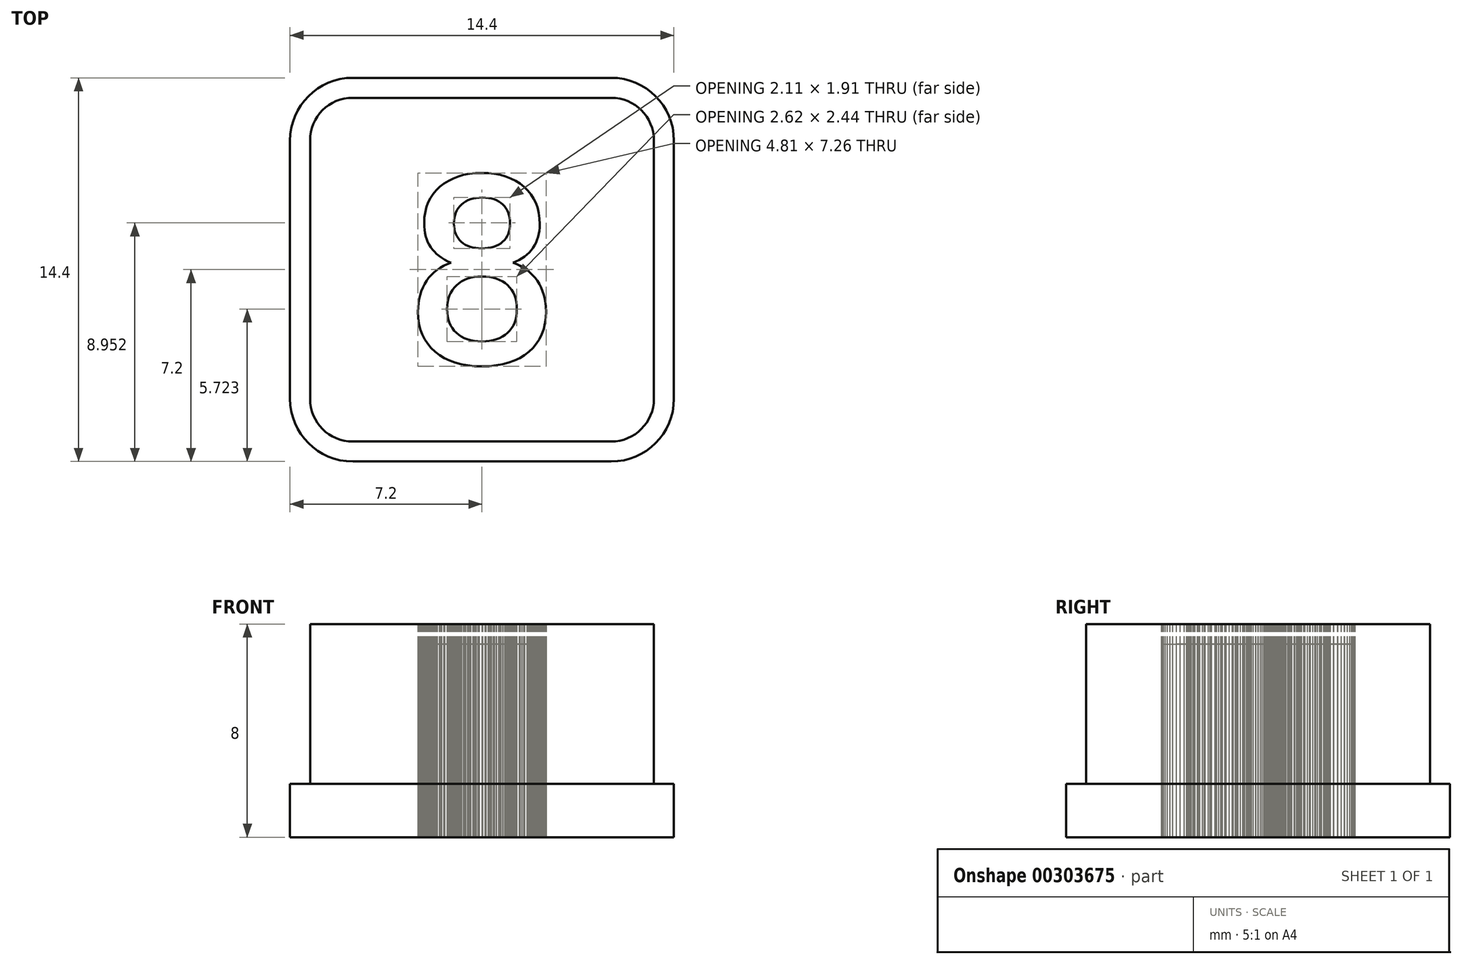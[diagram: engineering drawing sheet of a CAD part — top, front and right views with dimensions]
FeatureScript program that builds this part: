
annotation { "Feature Type Name" : "Feature", "Feature Type Description" : "" }
export const myFeature = defineFeature(function(context is Context, id is Id, definition is map)
    precondition{}
    {
        {
            var Q0;
            Q0=qCreatedBy(makeId("Top.planeOp"),FACE);
            var sketch = newSketch(context, id + "F0", { "sketchPlane" : qUnion([Q0])});
            skArc(sketch, "E0", {"start": v(4.85, -6.45) * mm, "mid": v(5.98, -5.98) * mm, "end": v(6.45, -4.85) * mm});
            skLineSegment(sketch, "E1", {"start": v(6.45, -4.85) * mm, "end": v(6.45, 4.85) * mm});
            skArc(sketch, "E2", {"start": v(6.45, 4.85) * mm, "mid": v(5.98, 5.98) * mm, "end": v(4.85, 6.45) * mm});
            skLineSegment(sketch, "E3", {"start": v(4.85, 6.45) * mm, "end": v(-4.85, 6.45) * mm});
            skArc(sketch, "E4", {"start": v(-4.85, 6.45) * mm, "mid": v(-5.98, 5.98) * mm, "end": v(-6.45, 4.85) * mm});
            skLineSegment(sketch, "E5", {"start": v(-6.45, 4.85) * mm, "end": v(-6.45, -4.85) * mm});
            skArc(sketch, "E6", {"start": v(-6.45, -4.85) * mm, "mid": v(-5.98, -5.98) * mm, "end": v(-4.85, -6.45) * mm});
            skLineSegment(sketch, "E7", {"start": v(-4.85, -6.45) * mm, "end": v(4.85, -6.45) * mm});
            skArc(sketch, "E8", {"start": v(-4.85, 7.2) * mm, "mid": v(-6.51, 6.51) * mm, "end": v(-7.2, 4.85) * mm});
            skLineSegment(sketch, "E9", {"start": v(-7.2, 4.85) * mm, "end": v(-7.2, -4.85) * mm});
            skArc(sketch, "E10", {"start": v(-7.2, -4.85) * mm, "mid": v(-6.51, -6.51) * mm, "end": v(-4.85, -7.2) * mm});
            skLineSegment(sketch, "E11", {"start": v(-4.85, -7.2) * mm, "end": v(4.85, -7.2) * mm});
            skArc(sketch, "E12", {"start": v(4.85, -7.2) * mm, "mid": v(6.51, -6.51) * mm, "end": v(7.2, -4.85) * mm});
            skLineSegment(sketch, "E13", {"start": v(7.2, -4.85) * mm, "end": v(7.2, 4.85) * mm});
            skArc(sketch, "E14", {"start": v(7.2, 4.85) * mm, "mid": v(6.51, 6.51) * mm, "end": v(4.85, 7.2) * mm});
            skLineSegment(sketch, "E15", {"start": v(4.85, 7.2) * mm, "end": v(-4.85, 7.2) * mm});
            skLineSegment(sketch, "E16", {"start": v(-1.16, 0.26) * mm, "end": v(-1.29, 0.32) * mm});
            skLineSegment(sketch, "E17", {"start": v(-1.29, 0.32) * mm, "end": v(-1.4, 0.38) * mm});
            skLineSegment(sketch, "E18", {"start": v(-1.4, 0.38) * mm, "end": v(-1.51, 0.45) * mm});
            skLineSegment(sketch, "E19", {"start": v(-1.51, 0.45) * mm, "end": v(-1.61, 0.52) * mm});
            skLineSegment(sketch, "E20", {"start": v(-1.61, 0.52) * mm, "end": v(-1.7, 0.6) * mm});
            skLineSegment(sketch, "E21", {"start": v(-1.7, 0.6) * mm, "end": v(-1.79, 0.67) * mm});
            skLineSegment(sketch, "E22", {"start": v(-1.79, 0.67) * mm, "end": v(-1.86, 0.76) * mm});
            skLineSegment(sketch, "E23", {"start": v(-1.86, 0.76) * mm, "end": v(-1.92, 0.85) * mm});
            skLineSegment(sketch, "E24", {"start": v(-1.92, 0.85) * mm, "end": v(-1.98, 0.94) * mm});
            skLineSegment(sketch, "E25", {"start": v(-1.98, 0.94) * mm, "end": v(-2.03, 1.04) * mm});
            skLineSegment(sketch, "E26", {"start": v(-2.03, 1.04) * mm, "end": v(-2.07, 1.14) * mm});
            skLineSegment(sketch, "E27", {"start": v(-2.07, 1.14) * mm, "end": v(-2.1, 1.26) * mm});
            skLineSegment(sketch, "E28", {"start": v(-2.1, 1.26) * mm, "end": v(-2.13, 1.37) * mm});
            skLineSegment(sketch, "E29", {"start": v(-2.13, 1.37) * mm, "end": v(-2.15, 1.5) * mm});
            skLineSegment(sketch, "E30", {"start": v(-2.15, 1.5) * mm, "end": v(-2.16, 1.62) * mm});
            skLineSegment(sketch, "E31", {"start": v(-2.16, 1.62) * mm, "end": v(-2.17, 1.75) * mm});
            skLineSegment(sketch, "E32", {"start": v(-2.17, 1.75) * mm, "end": v(-2.16, 1.96) * mm});
            skLineSegment(sketch, "E33", {"start": v(-2.16, 1.96) * mm, "end": v(-2.13, 2.16) * mm});
            skLineSegment(sketch, "E34", {"start": v(-2.13, 2.16) * mm, "end": v(-2.08, 2.34) * mm});
            skLineSegment(sketch, "E35", {"start": v(-2.08, 2.34) * mm, "end": v(-2.02, 2.52) * mm});
            skLineSegment(sketch, "E36", {"start": v(-2.02, 2.52) * mm, "end": v(-1.94, 2.68) * mm});
            skLineSegment(sketch, "E37", {"start": v(-1.94, 2.68) * mm, "end": v(-1.83, 2.83) * mm});
            skLineSegment(sketch, "E38", {"start": v(-1.83, 2.83) * mm, "end": v(-1.71, 2.98) * mm});
            skLineSegment(sketch, "E39", {"start": v(-1.71, 2.98) * mm, "end": v(-1.58, 3.11) * mm});
            skLineSegment(sketch, "E40", {"start": v(-1.58, 3.11) * mm, "end": v(-1.42, 3.23) * mm});
            skLineSegment(sketch, "E41", {"start": v(-1.42, 3.23) * mm, "end": v(-1.26, 3.34) * mm});
            skLineSegment(sketch, "E42", {"start": v(-1.26, 3.34) * mm, "end": v(-1.08, 3.43) * mm});
            skLineSegment(sketch, "E43", {"start": v(-1.08, 3.43) * mm, "end": v(-0.89, 3.5) * mm});
            skLineSegment(sketch, "E44", {"start": v(-0.89, 3.5) * mm, "end": v(-0.68, 3.56) * mm});
            skLineSegment(sketch, "E45", {"start": v(-0.68, 3.56) * mm, "end": v(-0.47, 3.6) * mm});
            skLineSegment(sketch, "E46", {"start": v(-0.47, 3.6) * mm, "end": v(-0.25, 3.62) * mm});
            skLineSegment(sketch, "E47", {"start": v(-0.25, 3.62) * mm, "end": v(0, 3.63) * mm});
            skLineSegment(sketch, "E48", {"start": v(0, 3.63) * mm, "end": v(0.24, 3.62) * mm});
            skLineSegment(sketch, "E49", {"start": v(0.24, 3.62) * mm, "end": v(0.47, 3.6) * mm});
            skLineSegment(sketch, "E50", {"start": v(0.47, 3.6) * mm, "end": v(0.68, 3.56) * mm});
            skLineSegment(sketch, "E51", {"start": v(0.68, 3.56) * mm, "end": v(0.89, 3.5) * mm});
            skLineSegment(sketch, "E52", {"start": v(0.89, 3.5) * mm, "end": v(1.08, 3.42) * mm});
            skLineSegment(sketch, "E53", {"start": v(1.08, 3.42) * mm, "end": v(1.26, 3.33) * mm});
            skLineSegment(sketch, "E54", {"start": v(1.26, 3.33) * mm, "end": v(1.43, 3.23) * mm});
            skLineSegment(sketch, "E55", {"start": v(1.43, 3.23) * mm, "end": v(1.58, 3.1) * mm});
            skLineSegment(sketch, "E56", {"start": v(1.58, 3.1) * mm, "end": v(1.72, 2.97) * mm});
            skLineSegment(sketch, "E57", {"start": v(1.72, 2.97) * mm, "end": v(1.84, 2.82) * mm});
            skLineSegment(sketch, "E58", {"start": v(1.84, 2.82) * mm, "end": v(1.94, 2.66) * mm});
            skLineSegment(sketch, "E59", {"start": v(1.94, 2.66) * mm, "end": v(2.02, 2.5) * mm});
            skLineSegment(sketch, "E60", {"start": v(2.02, 2.5) * mm, "end": v(2.09, 2.31) * mm});
            skLineSegment(sketch, "E61", {"start": v(2.09, 2.31) * mm, "end": v(2.13, 2.12) * mm});
            skLineSegment(sketch, "E62", {"start": v(2.13, 2.12) * mm, "end": v(2.16, 1.92) * mm});
            skLineSegment(sketch, "E63", {"start": v(2.16, 1.92) * mm, "end": v(2.17, 1.7) * mm});
            skLineSegment(sketch, "E64", {"start": v(2.17, 1.7) * mm, "end": v(2.16, 1.58) * mm});
            skLineSegment(sketch, "E65", {"start": v(2.16, 1.58) * mm, "end": v(2.15, 1.46) * mm});
            skLineSegment(sketch, "E66", {"start": v(2.15, 1.46) * mm, "end": v(2.13, 1.34) * mm});
            skLineSegment(sketch, "E67", {"start": v(2.13, 1.34) * mm, "end": v(2.1, 1.23) * mm});
            skLineSegment(sketch, "E68", {"start": v(2.1, 1.23) * mm, "end": v(2.07, 1.12) * mm});
            skLineSegment(sketch, "E69", {"start": v(2.07, 1.12) * mm, "end": v(2.02, 1.01) * mm});
            skLineSegment(sketch, "E70", {"start": v(2.02, 1.01) * mm, "end": v(1.97, 0.91) * mm});
            skLineSegment(sketch, "E71", {"start": v(1.97, 0.91) * mm, "end": v(1.91, 0.82) * mm});
            skLineSegment(sketch, "E72", {"start": v(1.91, 0.82) * mm, "end": v(1.84, 0.73) * mm});
            skLineSegment(sketch, "E73", {"start": v(1.84, 0.73) * mm, "end": v(1.77, 0.65) * mm});
            skLineSegment(sketch, "E74", {"start": v(1.77, 0.65) * mm, "end": v(1.69, 0.57) * mm});
            skLineSegment(sketch, "E75", {"start": v(1.69, 0.57) * mm, "end": v(1.6, 0.5) * mm});
            skLineSegment(sketch, "E76", {"start": v(1.6, 0.5) * mm, "end": v(1.5, 0.43) * mm});
            skLineSegment(sketch, "E77", {"start": v(1.5, 0.43) * mm, "end": v(1.4, 0.37) * mm});
            skLineSegment(sketch, "E78", {"start": v(1.4, 0.37) * mm, "end": v(1.28, 0.3) * mm});
            skLineSegment(sketch, "E79", {"start": v(1.28, 0.3) * mm, "end": v(1.16, 0.26) * mm});
            skLineSegment(sketch, "E80", {"start": v(1.16, 0.26) * mm, "end": v(1.3, 0.2) * mm});
            skLineSegment(sketch, "E81", {"start": v(1.3, 0.2) * mm, "end": v(1.44, 0.14) * mm});
            skLineSegment(sketch, "E82", {"start": v(1.44, 0.14) * mm, "end": v(1.56, 0.07) * mm});
            skLineSegment(sketch, "E83", {"start": v(1.56, 0.07) * mm, "end": v(1.68, 0) * mm});
            skLineSegment(sketch, "E84", {"start": v(1.68, 0) * mm, "end": v(1.79, -0.1) * mm});
            skLineSegment(sketch, "E85", {"start": v(1.79, -0.1) * mm, "end": v(1.9, -0.2) * mm});
            skLineSegment(sketch, "E86", {"start": v(1.9, -0.2) * mm, "end": v(1.99, -0.3) * mm});
            skLineSegment(sketch, "E87", {"start": v(1.99, -0.3) * mm, "end": v(2.07, -0.42) * mm});
            skLineSegment(sketch, "E88", {"start": v(2.07, -0.42) * mm, "end": v(2.15, -0.54) * mm});
            skLineSegment(sketch, "E89", {"start": v(2.15, -0.54) * mm, "end": v(2.22, -0.67) * mm});
            skLineSegment(sketch, "E90", {"start": v(2.22, -0.67) * mm, "end": v(2.27, -0.8) * mm});
            skLineSegment(sketch, "E91", {"start": v(2.27, -0.8) * mm, "end": v(2.32, -0.95) * mm});
            skLineSegment(sketch, "E92", {"start": v(2.32, -0.95) * mm, "end": v(2.36, -1.1) * mm});
            skLineSegment(sketch, "E93", {"start": v(2.36, -1.1) * mm, "end": v(2.38, -1.24) * mm});
            skLineSegment(sketch, "E94", {"start": v(2.38, -1.24) * mm, "end": v(2.4, -1.4) * mm});
            skLineSegment(sketch, "E95", {"start": v(2.4, -1.4) * mm, "end": v(2.4, -1.56) * mm});
            skLineSegment(sketch, "E96", {"start": v(2.4, -1.56) * mm, "end": v(2.4, -1.8) * mm});
            skLineSegment(sketch, "E97", {"start": v(2.4, -1.8) * mm, "end": v(2.36, -2.02) * mm});
            skLineSegment(sketch, "E98", {"start": v(2.36, -2.02) * mm, "end": v(2.31, -2.23) * mm});
            skLineSegment(sketch, "E99", {"start": v(2.31, -2.23) * mm, "end": v(2.24, -2.43) * mm});
            skLineSegment(sketch, "E100", {"start": v(2.24, -2.43) * mm, "end": v(2.15, -2.6) * mm});
            skLineSegment(sketch, "E101", {"start": v(2.15, -2.6) * mm, "end": v(2.04, -2.78) * mm});
            skLineSegment(sketch, "E102", {"start": v(2.04, -2.78) * mm, "end": v(1.91, -2.94) * mm});
            skLineSegment(sketch, "E103", {"start": v(1.91, -2.94) * mm, "end": v(1.76, -3.08) * mm});
            skLineSegment(sketch, "E104", {"start": v(1.76, -3.08) * mm, "end": v(1.6, -3.2) * mm});
            skLineSegment(sketch, "E105", {"start": v(1.6, -3.2) * mm, "end": v(1.41, -3.32) * mm});
            skLineSegment(sketch, "E106", {"start": v(1.41, -3.32) * mm, "end": v(1.22, -3.41) * mm});
            skLineSegment(sketch, "E107", {"start": v(1.22, -3.41) * mm, "end": v(1, -3.5) * mm});
            skLineSegment(sketch, "E108", {"start": v(1, -3.5) * mm, "end": v(0.77, -3.55) * mm});
            skLineSegment(sketch, "E109", {"start": v(0.77, -3.55) * mm, "end": v(0.53, -3.6) * mm});
            skLineSegment(sketch, "E110", {"start": v(0.53, -3.6) * mm, "end": v(0.27, -3.62) * mm});
            skLineSegment(sketch, "E111", {"start": v(0.27, -3.62) * mm, "end": v(0, -3.63) * mm});
            skLineSegment(sketch, "E112", {"start": v(0, -3.63) * mm, "end": v(-0.28, -3.62) * mm});
            skLineSegment(sketch, "E113", {"start": v(-0.28, -3.62) * mm, "end": v(-0.53, -3.6) * mm});
            skLineSegment(sketch, "E114", {"start": v(-0.53, -3.6) * mm, "end": v(-0.78, -3.55) * mm});
            skLineSegment(sketch, "E115", {"start": v(-0.78, -3.55) * mm, "end": v(-1, -3.5) * mm});
            skLineSegment(sketch, "E116", {"start": v(-1, -3.5) * mm, "end": v(-1.21, -3.41) * mm});
            skLineSegment(sketch, "E117", {"start": v(-1.21, -3.41) * mm, "end": v(-1.41, -3.32) * mm});
            skLineSegment(sketch, "E118", {"start": v(-1.41, -3.32) * mm, "end": v(-1.6, -3.2) * mm});
            skLineSegment(sketch, "E119", {"start": v(-1.6, -3.2) * mm, "end": v(-1.76, -3.08) * mm});
            skLineSegment(sketch, "E120", {"start": v(-1.76, -3.08) * mm, "end": v(-1.91, -2.94) * mm});
            skLineSegment(sketch, "E121", {"start": v(-1.91, -2.94) * mm, "end": v(-2.04, -2.78) * mm});
            skLineSegment(sketch, "E122", {"start": v(-2.04, -2.78) * mm, "end": v(-2.15, -2.61) * mm});
            skLineSegment(sketch, "E123", {"start": v(-2.15, -2.61) * mm, "end": v(-2.24, -2.43) * mm});
            skLineSegment(sketch, "E124", {"start": v(-2.24, -2.43) * mm, "end": v(-2.31, -2.24) * mm});
            skLineSegment(sketch, "E125", {"start": v(-2.31, -2.24) * mm, "end": v(-2.36, -2.03) * mm});
            skLineSegment(sketch, "E126", {"start": v(-2.36, -2.03) * mm, "end": v(-2.4, -1.81) * mm});
            skLineSegment(sketch, "E127", {"start": v(-2.4, -1.81) * mm, "end": v(-2.4, -1.58) * mm});
            skLineSegment(sketch, "E128", {"start": v(-2.4, -1.58) * mm, "end": v(-2.4, -1.41) * mm});
            skLineSegment(sketch, "E129", {"start": v(-2.4, -1.41) * mm, "end": v(-2.38, -1.25) * mm});
            skLineSegment(sketch, "E130", {"start": v(-2.38, -1.25) * mm, "end": v(-2.36, -1.1) * mm});
            skLineSegment(sketch, "E131", {"start": v(-2.36, -1.1) * mm, "end": v(-2.32, -0.95) * mm});
            skLineSegment(sketch, "E132", {"start": v(-2.32, -0.95) * mm, "end": v(-2.28, -0.8) * mm});
            skLineSegment(sketch, "E133", {"start": v(-2.28, -0.8) * mm, "end": v(-2.22, -0.67) * mm});
            skLineSegment(sketch, "E134", {"start": v(-2.22, -0.67) * mm, "end": v(-2.15, -0.54) * mm});
            skLineSegment(sketch, "E135", {"start": v(-2.15, -0.54) * mm, "end": v(-2.08, -0.41) * mm});
            skLineSegment(sketch, "E136", {"start": v(-2.08, -0.41) * mm, "end": v(-2, -0.3) * mm});
            skLineSegment(sketch, "E137", {"start": v(-2, -0.3) * mm, "end": v(-1.9, -0.2) * mm});
            skLineSegment(sketch, "E138", {"start": v(-1.9, -0.2) * mm, "end": v(-1.8, -0.1) * mm});
            skLineSegment(sketch, "E139", {"start": v(-1.8, -0.1) * mm, "end": v(-1.69, 0) * mm});
            skLineSegment(sketch, "E140", {"start": v(-1.69, 0) * mm, "end": v(-1.57, 0.07) * mm});
            skLineSegment(sketch, "E141", {"start": v(-1.57, 0.07) * mm, "end": v(-1.44, 0.14) * mm});
            skLineSegment(sketch, "E142", {"start": v(-1.44, 0.14) * mm, "end": v(-1.3, 0.2) * mm});
            skLineSegment(sketch, "E143", {"start": v(-1.3, 0.2) * mm, "end": v(-1.16, 0.26) * mm});
            skLineSegment(sketch, "E144", {"start": v(0.02, 2.7) * mm, "end": v(-0.1, 2.7) * mm});
            skLineSegment(sketch, "E145", {"start": v(-0.1, 2.7) * mm, "end": v(-0.22, 2.69) * mm});
            skLineSegment(sketch, "E146", {"start": v(-0.22, 2.69) * mm, "end": v(-0.33, 2.67) * mm});
            skLineSegment(sketch, "E147", {"start": v(-0.33, 2.67) * mm, "end": v(-0.43, 2.64) * mm});
            skLineSegment(sketch, "E148", {"start": v(-0.43, 2.64) * mm, "end": v(-0.52, 2.6) * mm});
            skLineSegment(sketch, "E149", {"start": v(-0.52, 2.6) * mm, "end": v(-0.61, 2.56) * mm});
            skLineSegment(sketch, "E150", {"start": v(-0.61, 2.56) * mm, "end": v(-0.7, 2.5) * mm});
            skLineSegment(sketch, "E151", {"start": v(-0.7, 2.5) * mm, "end": v(-0.77, 2.45) * mm});
            skLineSegment(sketch, "E152", {"start": v(-0.77, 2.45) * mm, "end": v(-0.83, 2.38) * mm});
            skLineSegment(sketch, "E153", {"start": v(-0.83, 2.38) * mm, "end": v(-0.9, 2.3) * mm});
            skLineSegment(sketch, "E154", {"start": v(-0.9, 2.3) * mm, "end": v(-0.94, 2.22) * mm});
            skLineSegment(sketch, "E155", {"start": v(-0.94, 2.22) * mm, "end": v(-0.98, 2.14) * mm});
            skLineSegment(sketch, "E156", {"start": v(-0.98, 2.14) * mm, "end": v(-1.01, 2.05) * mm});
            skLineSegment(sketch, "E157", {"start": v(-1.01, 2.05) * mm, "end": v(-1.04, 1.95) * mm});
            skLineSegment(sketch, "E158", {"start": v(-1.04, 1.95) * mm, "end": v(-1.05, 1.85) * mm});
            skLineSegment(sketch, "E159", {"start": v(-1.05, 1.85) * mm, "end": v(-1.05, 1.74) * mm});
            skLineSegment(sketch, "E160", {"start": v(-1.05, 1.74) * mm, "end": v(-1.05, 1.63) * mm});
            skLineSegment(sketch, "E161", {"start": v(-1.05, 1.63) * mm, "end": v(-1.04, 1.53) * mm});
            skLineSegment(sketch, "E162", {"start": v(-1.04, 1.53) * mm, "end": v(-1.01, 1.43) * mm});
            skLineSegment(sketch, "E163", {"start": v(-1.01, 1.43) * mm, "end": v(-0.98, 1.34) * mm});
            skLineSegment(sketch, "E164", {"start": v(-0.98, 1.34) * mm, "end": v(-0.95, 1.26) * mm});
            skLineSegment(sketch, "E165", {"start": v(-0.95, 1.26) * mm, "end": v(-0.9, 1.18) * mm});
            skLineSegment(sketch, "E166", {"start": v(-0.9, 1.18) * mm, "end": v(-0.84, 1.11) * mm});
            skLineSegment(sketch, "E167", {"start": v(-0.84, 1.11) * mm, "end": v(-0.77, 1.05) * mm});
            skLineSegment(sketch, "E168", {"start": v(-0.77, 1.05) * mm, "end": v(-0.7, 0.99) * mm});
            skLineSegment(sketch, "E169", {"start": v(-0.7, 0.99) * mm, "end": v(-0.62, 0.94) * mm});
            skLineSegment(sketch, "E170", {"start": v(-0.62, 0.94) * mm, "end": v(-0.54, 0.9) * mm});
            skLineSegment(sketch, "E171", {"start": v(-0.54, 0.9) * mm, "end": v(-0.44, 0.86) * mm});
            skLineSegment(sketch, "E172", {"start": v(-0.44, 0.86) * mm, "end": v(-0.34, 0.83) * mm});
            skLineSegment(sketch, "E173", {"start": v(-0.34, 0.83) * mm, "end": v(-0.24, 0.81) * mm});
            skLineSegment(sketch, "E174", {"start": v(-0.24, 0.81) * mm, "end": v(-0.13, 0.8) * mm});
            skLineSegment(sketch, "E175", {"start": v(-0.13, 0.8) * mm, "end": v(0, 0.8) * mm});
            skLineSegment(sketch, "E176", {"start": v(0, 0.8) * mm, "end": v(0.11, 0.8) * mm});
            skLineSegment(sketch, "E177", {"start": v(0.11, 0.8) * mm, "end": v(0.23, 0.81) * mm});
            skLineSegment(sketch, "E178", {"start": v(0.23, 0.81) * mm, "end": v(0.34, 0.83) * mm});
            skLineSegment(sketch, "E179", {"start": v(0.34, 0.83) * mm, "end": v(0.44, 0.86) * mm});
            skLineSegment(sketch, "E180", {"start": v(0.44, 0.86) * mm, "end": v(0.53, 0.9) * mm});
            skLineSegment(sketch, "E181", {"start": v(0.53, 0.9) * mm, "end": v(0.62, 0.94) * mm});
            skLineSegment(sketch, "E182", {"start": v(0.62, 0.94) * mm, "end": v(0.7, 0.99) * mm});
            skLineSegment(sketch, "E183", {"start": v(0.7, 0.99) * mm, "end": v(0.77, 1.04) * mm});
            skLineSegment(sketch, "E184", {"start": v(0.77, 1.04) * mm, "end": v(0.84, 1.1) * mm});
            skLineSegment(sketch, "E185", {"start": v(0.84, 1.1) * mm, "end": v(0.9, 1.18) * mm});
            skLineSegment(sketch, "E186", {"start": v(0.9, 1.18) * mm, "end": v(0.95, 1.26) * mm});
            skLineSegment(sketch, "E187", {"start": v(0.95, 1.26) * mm, "end": v(0.98, 1.34) * mm});
            skLineSegment(sketch, "E188", {"start": v(0.98, 1.34) * mm, "end": v(1.01, 1.43) * mm});
            skLineSegment(sketch, "E189", {"start": v(1.01, 1.43) * mm, "end": v(1.04, 1.53) * mm});
            skLineSegment(sketch, "E190", {"start": v(1.04, 1.53) * mm, "end": v(1.05, 1.63) * mm});
            skLineSegment(sketch, "E191", {"start": v(1.05, 1.63) * mm, "end": v(1.05, 1.74) * mm});
            skLineSegment(sketch, "E192", {"start": v(1.05, 1.74) * mm, "end": v(1.05, 1.85) * mm});
            skLineSegment(sketch, "E193", {"start": v(1.05, 1.85) * mm, "end": v(1.04, 1.95) * mm});
            skLineSegment(sketch, "E194", {"start": v(1.04, 1.95) * mm, "end": v(1.02, 2.05) * mm});
            skLineSegment(sketch, "E195", {"start": v(1.02, 2.05) * mm, "end": v(0.98, 2.14) * mm});
            skLineSegment(sketch, "E196", {"start": v(0.98, 2.14) * mm, "end": v(0.95, 2.23) * mm});
            skLineSegment(sketch, "E197", {"start": v(0.95, 2.23) * mm, "end": v(0.9, 2.3) * mm});
            skLineSegment(sketch, "E198", {"start": v(0.9, 2.3) * mm, "end": v(0.84, 2.38) * mm});
            skLineSegment(sketch, "E199", {"start": v(0.84, 2.38) * mm, "end": v(0.78, 2.45) * mm});
            skLineSegment(sketch, "E200", {"start": v(0.78, 2.45) * mm, "end": v(0.7, 2.5) * mm});
            skLineSegment(sketch, "E201", {"start": v(0.7, 2.5) * mm, "end": v(0.63, 2.56) * mm});
            skLineSegment(sketch, "E202", {"start": v(0.63, 2.56) * mm, "end": v(0.54, 2.6) * mm});
            skLineSegment(sketch, "E203", {"start": v(0.54, 2.6) * mm, "end": v(0.45, 2.64) * mm});
            skLineSegment(sketch, "E204", {"start": v(0.45, 2.64) * mm, "end": v(0.35, 2.67) * mm});
            skLineSegment(sketch, "E205", {"start": v(0.35, 2.67) * mm, "end": v(0.25, 2.7) * mm});
            skLineSegment(sketch, "E206", {"start": v(0.25, 2.7) * mm, "end": v(0.13, 2.7) * mm});
            skLineSegment(sketch, "E207", {"start": v(0.13, 2.7) * mm, "end": v(0.02, 2.7) * mm});
            skLineSegment(sketch, "E208", {"start": v(0, -2.7) * mm, "end": v(0.14, -2.7) * mm});
            skLineSegment(sketch, "E209", {"start": v(0.14, -2.7) * mm, "end": v(0.28, -2.68) * mm});
            skLineSegment(sketch, "E210", {"start": v(0.28, -2.68) * mm, "end": v(0.42, -2.65) * mm});
            skLineSegment(sketch, "E211", {"start": v(0.42, -2.65) * mm, "end": v(0.54, -2.62) * mm});
            skLineSegment(sketch, "E212", {"start": v(0.54, -2.62) * mm, "end": v(0.66, -2.57) * mm});
            skLineSegment(sketch, "E213", {"start": v(0.66, -2.57) * mm, "end": v(0.77, -2.52) * mm});
            skLineSegment(sketch, "E214", {"start": v(0.77, -2.52) * mm, "end": v(0.87, -2.45) * mm});
            skLineSegment(sketch, "E215", {"start": v(0.87, -2.45) * mm, "end": v(0.96, -2.37) * mm});
            skLineSegment(sketch, "E216", {"start": v(0.96, -2.37) * mm, "end": v(1.04, -2.29) * mm});
            skLineSegment(sketch, "E217", {"start": v(1.04, -2.29) * mm, "end": v(1.11, -2.2) * mm});
            skLineSegment(sketch, "E218", {"start": v(1.11, -2.2) * mm, "end": v(1.17, -2.1) * mm});
            skLineSegment(sketch, "E219", {"start": v(1.17, -2.1) * mm, "end": v(1.22, -1.99) * mm});
            skLineSegment(sketch, "E220", {"start": v(1.22, -1.99) * mm, "end": v(1.26, -1.87) * mm});
            skLineSegment(sketch, "E221", {"start": v(1.26, -1.87) * mm, "end": v(1.29, -1.75) * mm});
            skLineSegment(sketch, "E222", {"start": v(1.29, -1.75) * mm, "end": v(1.3, -1.62) * mm});
            skLineSegment(sketch, "E223", {"start": v(1.3, -1.62) * mm, "end": v(1.3, -1.48) * mm});
            skLineSegment(sketch, "E224", {"start": v(1.3, -1.48) * mm, "end": v(1.3, -1.34) * mm});
            skLineSegment(sketch, "E225", {"start": v(1.3, -1.34) * mm, "end": v(1.29, -1.21) * mm});
            skLineSegment(sketch, "E226", {"start": v(1.29, -1.21) * mm, "end": v(1.26, -1.09) * mm});
            skLineSegment(sketch, "E227", {"start": v(1.26, -1.09) * mm, "end": v(1.22, -0.97) * mm});
            skLineSegment(sketch, "E228", {"start": v(1.22, -0.97) * mm, "end": v(1.17, -0.86) * mm});
            skLineSegment(sketch, "E229", {"start": v(1.17, -0.86) * mm, "end": v(1.11, -0.76) * mm});
            skLineSegment(sketch, "E230", {"start": v(1.11, -0.76) * mm, "end": v(1.04, -0.67) * mm});
            skLineSegment(sketch, "E231", {"start": v(1.04, -0.67) * mm, "end": v(0.96, -0.58) * mm});
            skLineSegment(sketch, "E232", {"start": v(0.96, -0.58) * mm, "end": v(0.87, -0.5) * mm});
            skLineSegment(sketch, "E233", {"start": v(0.87, -0.5) * mm, "end": v(0.77, -0.44) * mm});
            skLineSegment(sketch, "E234", {"start": v(0.77, -0.44) * mm, "end": v(0.66, -0.39) * mm});
            skLineSegment(sketch, "E235", {"start": v(0.66, -0.39) * mm, "end": v(0.54, -0.34) * mm});
            skLineSegment(sketch, "E236", {"start": v(0.54, -0.34) * mm, "end": v(0.42, -0.3) * mm});
            skLineSegment(sketch, "E237", {"start": v(0.42, -0.3) * mm, "end": v(0.28, -0.28) * mm});
            skLineSegment(sketch, "E238", {"start": v(0.28, -0.28) * mm, "end": v(0.14, -0.26) * mm});
            skLineSegment(sketch, "E239", {"start": v(0.14, -0.26) * mm, "end": v(0, -0.26) * mm});
            skLineSegment(sketch, "E240", {"start": v(0, -0.26) * mm, "end": v(-0.15, -0.26) * mm});
            skLineSegment(sketch, "E241", {"start": v(-0.15, -0.26) * mm, "end": v(-0.3, -0.28) * mm});
            skLineSegment(sketch, "E242", {"start": v(-0.3, -0.28) * mm, "end": v(-0.42, -0.3) * mm});
            skLineSegment(sketch, "E243", {"start": v(-0.42, -0.3) * mm, "end": v(-0.55, -0.34) * mm});
            skLineSegment(sketch, "E244", {"start": v(-0.55, -0.34) * mm, "end": v(-0.66, -0.39) * mm});
            skLineSegment(sketch, "E245", {"start": v(-0.66, -0.39) * mm, "end": v(-0.77, -0.44) * mm});
            skLineSegment(sketch, "E246", {"start": v(-0.77, -0.44) * mm, "end": v(-0.87, -0.51) * mm});
            skLineSegment(sketch, "E247", {"start": v(-0.87, -0.51) * mm, "end": v(-0.96, -0.59) * mm});
            skLineSegment(sketch, "E248", {"start": v(-0.96, -0.59) * mm, "end": v(-1.04, -0.67) * mm});
            skLineSegment(sketch, "E249", {"start": v(-1.04, -0.67) * mm, "end": v(-1.11, -0.77) * mm});
            skLineSegment(sketch, "E250", {"start": v(-1.11, -0.77) * mm, "end": v(-1.17, -0.87) * mm});
            skLineSegment(sketch, "E251", {"start": v(-1.17, -0.87) * mm, "end": v(-1.22, -0.98) * mm});
            skLineSegment(sketch, "E252", {"start": v(-1.22, -0.98) * mm, "end": v(-1.26, -1.1) * mm});
            skLineSegment(sketch, "E253", {"start": v(-1.26, -1.1) * mm, "end": v(-1.29, -1.21) * mm});
            skLineSegment(sketch, "E254", {"start": v(-1.29, -1.21) * mm, "end": v(-1.3, -1.34) * mm});
            skLineSegment(sketch, "E255", {"start": v(-1.3, -1.34) * mm, "end": v(-1.3, -1.48) * mm});
            skLineSegment(sketch, "E256", {"start": v(-1.3, -1.48) * mm, "end": v(-1.3, -1.62) * mm});
            skLineSegment(sketch, "E257", {"start": v(-1.3, -1.62) * mm, "end": v(-1.29, -1.75) * mm});
            skLineSegment(sketch, "E258", {"start": v(-1.29, -1.75) * mm, "end": v(-1.26, -1.87) * mm});
            skLineSegment(sketch, "E259", {"start": v(-1.26, -1.87) * mm, "end": v(-1.22, -1.99) * mm});
            skLineSegment(sketch, "E260", {"start": v(-1.22, -1.99) * mm, "end": v(-1.17, -2.1) * mm});
            skLineSegment(sketch, "E261", {"start": v(-1.17, -2.1) * mm, "end": v(-1.11, -2.2) * mm});
            skLineSegment(sketch, "E262", {"start": v(-1.11, -2.2) * mm, "end": v(-1.04, -2.29) * mm});
            skLineSegment(sketch, "E263", {"start": v(-1.04, -2.29) * mm, "end": v(-0.96, -2.37) * mm});
            skLineSegment(sketch, "E264", {"start": v(-0.96, -2.37) * mm, "end": v(-0.87, -2.45) * mm});
            skLineSegment(sketch, "E265", {"start": v(-0.87, -2.45) * mm, "end": v(-0.77, -2.52) * mm});
            skLineSegment(sketch, "E266", {"start": v(-0.77, -2.52) * mm, "end": v(-0.67, -2.57) * mm});
            skLineSegment(sketch, "E267", {"start": v(-0.67, -2.57) * mm, "end": v(-0.55, -2.62) * mm});
            skLineSegment(sketch, "E268", {"start": v(-0.55, -2.62) * mm, "end": v(-0.43, -2.65) * mm});
            skLineSegment(sketch, "E269", {"start": v(-0.43, -2.65) * mm, "end": v(-0.3, -2.68) * mm});
            skLineSegment(sketch, "E270", {"start": v(-0.3, -2.68) * mm, "end": v(-0.16, -2.7) * mm});
            skLineSegment(sketch, "E271", {"start": v(-0.16, -2.7) * mm, "end": v(0, -2.7) * mm});
            skSolve(sketch);
        }
        {
            var Q0;
            Q0=makeQuery(id+"F0.imprint","IMPRINT",FACE,{"disambiguationData":[TD([[makeQuery(id+"F0.imprint","IMPRINT",EDGE,{"derivedFrom":sQuery(id+"F0.wireOp",EDGE,"E0")}),-1.0]])]});
            extrude(context, id + "F1", {"entities" : qUnion([Q0]), "depth" : 2 * mm});
        }
        {
            var Q0;
            Q0=makeQuery(id+"F0.imprint","IMPRINT",FACE,{"disambiguationData":[TD([[makeQuery(id+"F0.imprint","IMPRINT",EDGE,{"derivedFrom":sQuery(id+"F0.wireOp",EDGE,"E0")}),1.0]])]});
            var Q1;
            Q1=makeQuery(id+"F0.imprint","IMPRINT",FACE,{"disambiguationData":[TD([[makeQuery(id+"F0.imprint","IMPRINT",EDGE,{"derivedFrom":sQuery(id+"F0.wireOp",EDGE,"E144")}),1.0]])]});
            var Q2;
            Q2=makeQuery(id+"F0.imprint","IMPRINT",FACE,{"disambiguationData":[TD([[makeQuery(id+"F0.imprint","IMPRINT",EDGE,{"derivedFrom":sQuery(id+"F0.wireOp",EDGE,"E208")}),1.0]])]});
            extrude(context, id + "F2", {"entities" : qUnion([Q0, Q1, Q2]), "operationType" : NewBodyOperationType.ADD, "depth" : 8 * mm});
        }
        {
            var Q0;
            Q0=makeQuery(id+"F0.imprint","IMPRINT",FACE,{"disambiguationData":[TD([[makeQuery(id+"F0.imprint","IMPRINT",EDGE,{"derivedFrom":sQuery(id+"F0.wireOp",EDGE,"E16")}),-1.0]])]});
            extrude(context, id + "F3", {"entities" : qUnion([Q0]), "depth" : 7.25 * mm});
        }
    });
